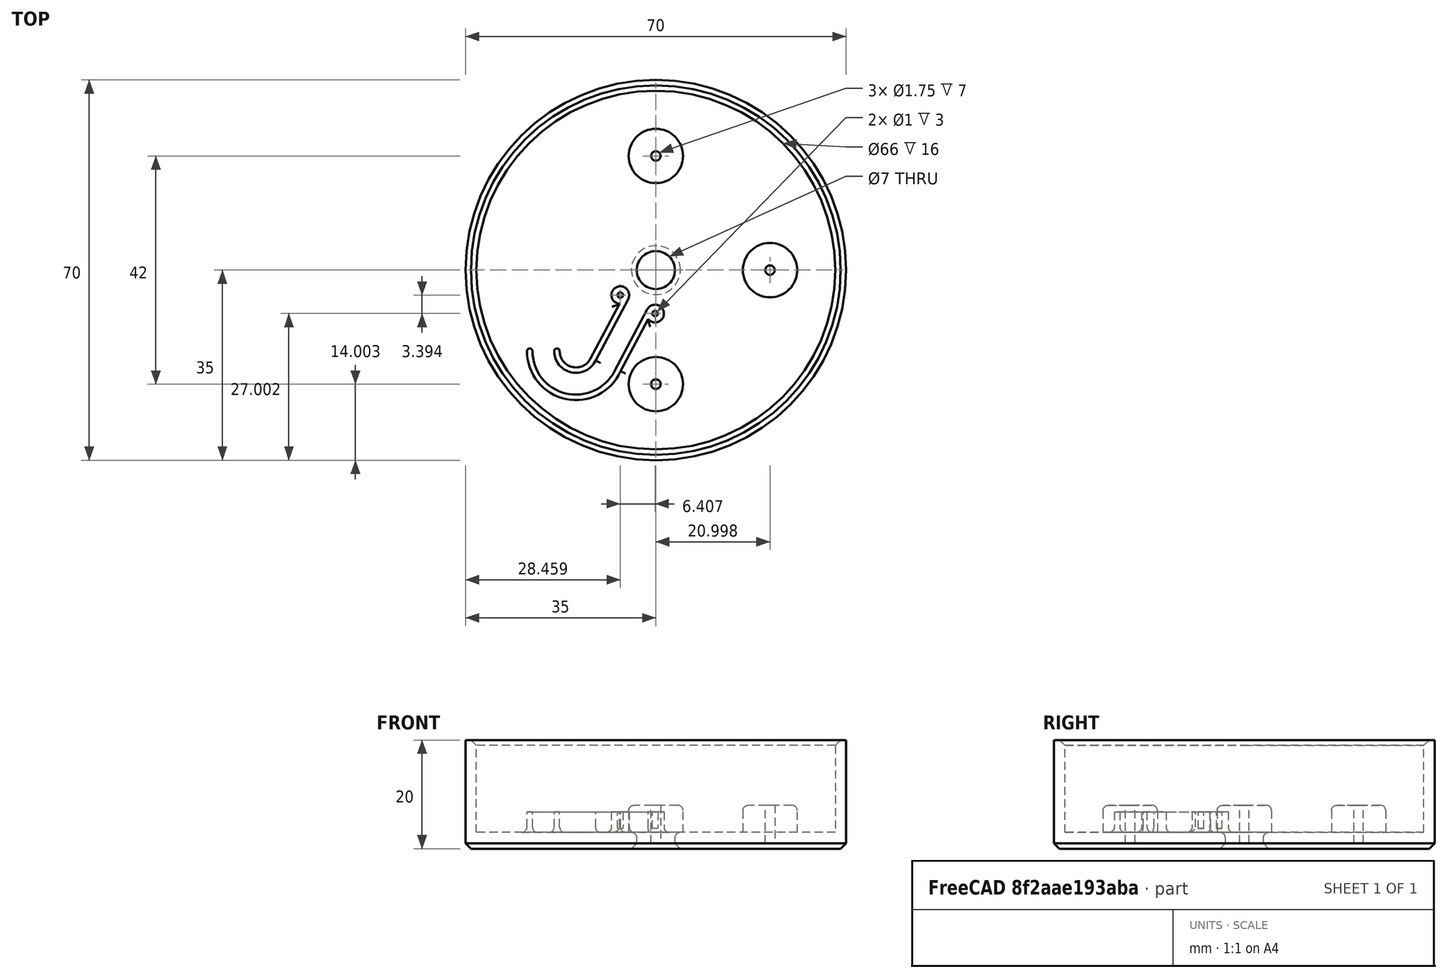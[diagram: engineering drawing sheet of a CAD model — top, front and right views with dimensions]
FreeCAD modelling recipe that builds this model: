
FCSTD DOCUMENT  (FreeCAD 0.21R33771 (Git))
Label: Webcam mount
License: All rights reserved
LicenseURL: http://en.wikipedia.org/wiki/All_rights_reserved
objects: Sketcher::SketchObject×8, PartDesign::Pocket×4, PartDesign::Fillet×4, PartDesign::Pad×3, PartDesign::Body×2, Part::Feature×2, PartDesign::Chamfer×1, App::Part×1, Mesh::Feature×1, Part::Refine×1
note: 37 computed .brp shape members not serialized (recipe doc carries the construction recipe); baked Part::Feature solids carry a one-line shape summary decoded from their .brp

FEATURE [Sketcher::SketchObject] Sketch001
  FullyConstrained = true
  MapMode = 5
  Support = -> [XY_Plane]
  sketch-geometry (1):
    g0: Circle CenterX=0 CenterY=0 CenterZ=0 NormalX=0 NormalY=0 NormalZ=1 AngleXU=0 Radius=35
  constraints (2):
    c: Coincident(g0,g-1)
    c: Diameter(g0) = 70
FEATURE [PartDesign::Pad] Pad
  Direction = (0,0,1)
  Length = 20
  Length2 = 10
  Profile = -> Sketch001
  ReferenceAxis = -> Sketch001 [N_Axis]
  Type = 0
FEATURE [Sketcher::SketchObject] Sketch
  FullyConstrained = true
  MapMode = 5
  Placement = pos=(0,0,20) rot=(0,0,1;0rad)
  Support = -> [Pad]
  sketch-geometry (1):
    g0: Circle CenterX=0 CenterY=0 CenterZ=0 NormalX=0 NormalY=0 NormalZ=1 AngleXU=0 Radius=33
  constraints (2):
    c: Coincident(g0,g-1)
    c: Diameter(g0) = 66
FEATURE [PartDesign::Pocket] Pocket
  BaseFeature = -> Pad
  Direction = (0,0,-1)
  Length = 17
  Length2 = 5
  Profile = -> Sketch
  ReferenceAxis = -> Sketch [N_Axis]
  Type = 0
FEATURE [Sketcher::SketchObject] Sketch002
  FullyConstrained = false
  MapMode = 5
  Placement = pos=(0,0,3) rot=(0,0,1;0rad)
  Support = -> [Pocket]
  sketch-geometry (4):
    g0: Circle CenterX=-0.00194019 CenterY=0.00345167 CenterZ=0 NormalX=0 NormalY=0 NormalZ=1 AngleXU=0 Radius=21
    g1: Circle CenterX=0 CenterY=21.0035 CenterZ=0 NormalX=0 NormalY=0 NormalZ=1 AngleXU=0 Radius=5
    g2: Circle CenterX=20.9981 CenterY=0 CenterZ=0 NormalX=0 NormalY=0 NormalZ=1 AngleXU=0 Radius=5
    g3: Circle CenterX=0 CenterY=-20.9965 CenterZ=0 NormalX=0 NormalY=0 NormalZ=1 AngleXU=0 Radius=5
  constraints (10):
    c: Diameter(g0) = 42
    c: PointOnObject(g1,g0)
    c: PointOnObject(g2,g0)
    c: PointOnObject(g3,g0)
    c: PointOnObject(g3,g-2)
    c: PointOnObject(g2,g-1)
    c: PointOnObject(g1,g-2)
    c: Equal(g1,g2)
    c: Equal(g2,g3)
    c: Diameter(g1) = 10
FEATURE [PartDesign::Pad] Pad001
  BaseFeature = -> Pocket
  Direction = (0,0,1)
  Length = 5
  Length2 = 10
  Profile = -> Sketch002
  ReferenceAxis = -> Sketch002 [N_Axis]
  Type = 0
FEATURE [Sketcher::SketchObject] Sketch003
  ExternalGeometry = -> [Pad001]
  FullyConstrained = true
  MapMode = 5
  Placement = pos=(0,0,8) rot=(0,0,1;0rad)
  Support = -> [Pad001]
  sketch-geometry (3):
    g0: Circle CenterX=0 CenterY=21.0035 CenterZ=0 NormalX=0 NormalY=0 NormalZ=1 AngleXU=0 Radius=0.875
    g1: Circle CenterX=0 CenterY=-20.9965 CenterZ=0 NormalX=0 NormalY=0 NormalZ=1 AngleXU=0 Radius=0.875
    g2: Circle CenterX=20.9981 CenterY=0 CenterZ=0 NormalX=0 NormalY=0 NormalZ=1 AngleXU=0 Radius=0.875
  constraints (6):
    c: Coincident(g0,g-3)
    c: Coincident(g1,g-4)
    c: Coincident(g2,g-5)
    c: Equal(g0,g1)
    c: Equal(g1,g2)
    c: Diameter(g0) = 1.75
FEATURE [PartDesign::Pocket] Pocket001
  BaseFeature = -> Pad001
  Direction = (0,0,-1)
  Length = 7
  Length2 = 5
  Profile = -> Sketch003
  ReferenceAxis = -> Sketch003 [N_Axis]
  Type = 0
FEATURE [Sketcher::SketchObject] Sketch004
  FullyConstrained = true
  MapMode = 5
  Placement = pos=(0,0,3) rot=(0,0,1;0rad)
  Support = -> [Pocket001]
  sketch-geometry (1):
    g0: Circle CenterX=0 CenterY=0 CenterZ=0 NormalX=0 NormalY=0 NormalZ=1 AngleXU=0 Radius=3.5
  constraints (3):
    c: PointOnObject(g0,g-1)
    c: Diameter(g0) = 7
    c: PointOnObject(g0,g-2)
FEATURE [PartDesign::Pocket] Pocket002
  BaseFeature = -> Pocket001
  Direction = (0,0,-1)
  Length = 10
  Length2 = 5
  Profile = -> Sketch004
  ReferenceAxis = -> Sketch004 [N_Axis]
  Type = 0
FEATURE [PartDesign::Chamfer] Chamfer
  Angle = 45
  Base = -> Pocket002 [Edge2,Edge5,Edge4]
  BaseFeature = -> Pocket002
  ChamferType = 0
  FlipDirection = false
  Size = 1
  Size2 = 1
  SupportTransform = false
  UseAllEdges = false
FEATURE [Sketcher::SketchObject] Sketch005
  ExternalGeometry = -> [Chamfer]
  FullyConstrained = false
  MapMode = 5
  Placement = pos=(0,0,3) rot=(0,0,1;0rad)
  Support = -> [Chamfer]
  sketch-geometry (21):
    g0: LineSegment StartX=0 StartY=0 StartZ=0 EndX=-12.3375 EndY=-23.2904 EndZ=0
    g1: LineSegment StartX=-3.33785 StartY=-6.30109 StartZ=0 EndX=-5.10519 EndY=-5.36488 EndZ=0
    g2: LineSegment StartX=-3.33785 StartY=-6.30109 StartZ=0 EndX=-1.5705 EndY=-7.2373 EndZ=0
    g3: ArcOfCircle CenterX=-0.134531 CenterY=-7.99797 CenterZ=0 NormalX=0 NormalY=0 NormalZ=1 AngleXU=0 Radius=1.625 StartAngle=3.81788 EndAngle=8.93763
    g4: ArcOfCircle CenterX=-6.54116 CenterY=-4.60421 CenterZ=0 NormalX=0 NormalY=0 NormalZ=1 AngleXU=0 Radius=1.625 StartAngle=5.79576 EndAngle=10.9054
    g5: ArcOfCircle CenterX=-14.6925 CenterY=-14.9185 CenterZ=0 NormalX=0 NormalY=0 NormalZ=1 AngleXU=0 Radius=4 StartAngle=3.14159 EndAngle=5.83833
    g6: LineSegment StartX=-11.1578 StartY=-16.7909 StartZ=0 EndX=-9.3905 EndY=-17.7271 EndZ=0
    g7: LineSegment StartX=-9.3905 StartY=-17.7271 StartZ=0 EndX=-7.62315 EndY=-18.6633 EndZ=0
    g8: LineSegment StartX=-14.9937 StartY=-18.9071 StartZ=0 EndX=-14.9184 EndY=-17.91 EndZ=0
    g9: ArcOfCircle CenterX=-14.6925 CenterY=-14.9185 CenterZ=0 NormalX=0 NormalY=0 NormalZ=1 AngleXU=0 Radius=3 StartAngle=3.14159 EndAngle=5.79576
    g10: LineSegment StartX=-8.32768 StartY=-19.765 StartZ=0 EndX=-7.53208 EndY=-20.3708 EndZ=0
    g11: LineSegment StartX=-11.0819 StartY=-16.6398 StartZ=0 EndX=-5.10541 EndY=-5.36528 EndZ=0
    g12: LineSegment StartX=-7.62315 StartY=-18.6633 StartZ=0 EndX=-1.5705 EndY=-7.2373 EndZ=0
    g13: LineSegment StartX=-6.48386 StartY=-18.6087 StartZ=0 EndX=-1.40187 EndY=-9.01506 EndZ=0
    g14: LineSegment StartX=-12.0419 StartY=-16.3235 StartZ=0 EndX=-6.68757 EndY=-6.2226 EndZ=0
    g15: LineSegment StartX=-14.6925 StartY=-14.9185 StartZ=0 EndX=-23.6925 EndY=-14.9185 EndZ=0
    g16: ArcOfCircle CenterX=-23.1925 CenterY=-14.9185 CenterZ=0 NormalX=0 NormalY=0 NormalZ=1 AngleXU=0 Radius=0.5 StartAngle=0 EndAngle=3.14159
    g17: ArcOfCircle CenterX=-18.1925 CenterY=-14.9185 CenterZ=0 NormalX=0 NormalY=0 NormalZ=1 AngleXU=0 Radius=0.5 StartAngle=-9e-16 EndAngle=3.14159
    g18: GeomPoint X=-22.6925 Y=-14.9185 Z=0
    g19: ArcOfCircle CenterX=-14.6925 CenterY=-14.9185 CenterZ=0 NormalX=0 NormalY=0 NormalZ=1 AngleXU=0 Radius=9 StartAngle=3.14159 EndAngle=5.86071
    g20: ArcOfCircle CenterX=-14.6925 CenterY=-14.9185 CenterZ=0 NormalX=0 NormalY=0 NormalZ=1 AngleXU=0 Radius=8 StartAngle=3.14159 EndAngle=5.79604
  constraints (45):
    c: Coincident(g0,g-3)
    c: Coincident(g2,g1)
    c: PointOnObject(g1,g0)
    c: Perpendicular(g0,g1)
    c: Perpendicular(g0,g2)
    c: Equal(g1,g2)
    c: Distance(g1,g2) = 4
    c: PointOnObject(g1,g4)
    c: Perpendicular(g4,g1)
    c: Equal(g4,g3)
    c: Diameter(g3) = 3.25
    c: Diameter(g5) = 8
    c: PointOnObject(g6,g5)
    c: Coincident(g7,g6)
    c: Perpendicular(g5,g6)
    c: Equal(g6,g7)
    c: PointOnObject(g6,g0)
    c: Perpendicular(g0,g6)
    c: PointOnObject(g8,g5)
    c: Perpendicular(g5,g8)
    c: Distance(g8) = 1  'cable guide wall thickness'
    c: Coincident(g9,g5)
    c: PointOnObject(g8,g9)
    c: Equal(g8,g10)
    c: Tangent(g12,g3) = 1.5708
    c: Parallel(g14,g11)
    c: Parallel(g12,g13)
    c: Coincident(g15,g5)
    c: Horizontal(g15)
    c: PointOnObject(g16,g15)
    c: PointOnObject(g17,g15)
    c: PointOnObject(g18,g16)
    c: Coincident(g19,g13)
    c: Coincident(g20,g12) = -1.5708
    c: Perpendicular(g3,g2) = 1.5708
    c: Coincident(g3,g13)
    c: Coincident(g4,g14)
    c: Tangent(g4,g11) = -1.5708
    c: Tangent(g16,g19) = -1.5708
    c: Tangent(g16,g20) = 1.5708
    c: Tangent(g17,g9) = 1.5708
    c: Tangent(g5,g17) = -1.5708
    c: Tangent(g9,g14) = -1.5708
    c: PointOnObject(g9,g15)
    c: Coincident(g5,g11)
FEATURE [PartDesign::Pad] Pad002
  BaseFeature = -> Chamfer
  Direction = (0,0,1)
  Length = 3.75
  Length2 = 10
  Profile = -> Sketch005
  ReferenceAxis = -> Sketch005 [N_Axis]
  Type = 0
FEATURE [Sketcher::SketchObject] Sketch006
  ExternalGeometry = -> [Pad002]
  FullyConstrained = true
  MapMode = 5
  Placement = pos=(0,0,6.75) rot=(0,0,1;0rad)
  Support = -> [Pad002]
  sketch-geometry (2):
    g0: Circle CenterX=-6.54116 CenterY=-4.60421 CenterZ=0 NormalX=0 NormalY=0 NormalZ=1 AngleXU=0 Radius=0.5
    g1: Circle CenterX=-0.134531 CenterY=-7.99797 CenterZ=0 NormalX=0 NormalY=0 NormalZ=1 AngleXU=0 Radius=0.5
  constraints (4):
    c: Coincident(g0,g-3)
    c: Coincident(g1,g-4)
    c: Equal(g0,g1)
    c: Diameter(g0) = 1
FEATURE [PartDesign::Pocket] Pocket003
  BaseFeature = -> Pad002
  Direction = (0,0,-1)
  Length = 3
  Length2 = 5
  Profile = -> Sketch006
  ReferenceAxis = -> Sketch006 [N_Axis]
  Type = 0
FEATURE [PartDesign::Fillet] Fillet
  Base = -> Pocket003 [Edge15]
  BaseFeature = -> Pocket003
  Radius = 1
  SupportTransform = false
  UseAllEdges = false
FEATURE [PartDesign::Body] Body001  label="Body"
  Origin = -> Origin002
FEATURE [PartDesign::Fillet] Fillet001
  Base = -> Fillet [Edge21]
  BaseFeature = -> Fillet
  Radius = 1
  SupportTransform = false
  UseAllEdges = false
FEATURE [PartDesign::Fillet] Fillet002
  Base = -> Fillet001 [Edge13]
  BaseFeature = -> Fillet001
  Radius = 1
  SupportTransform = false
  UseAllEdges = false
FEATURE [PartDesign::Fillet] Fillet003
  Base = -> Fillet002 [Edge49,Edge47,Edge51]
  BaseFeature = -> Fillet002
  Radius = 1
  SupportTransform = false
  UseAllEdges = false
FEATURE [PartDesign::Body] Body  label="Webcam Mount"
  Group = -> [Sketch,Sketch001,Pad,Pocket,Sketch002,Pad001,Sketch003,Pocket001,Sketch004,Pocket002,Chamfer,Sketch005,Pad002,Sketch006,Pocket003,Fillet,Fillet001,Fillet002,Fillet003]
  Origin = -> Origin
  Tip = -> Fillet003
FEATURE [App::Part] Part
  Group = -> [Body,Body001]
  Origin = -> Origin001
FEATURE [Mesh::Feature] Head_v1
FEATURE [Part::Feature] Head_v002
  shape: large baked B-rep (101 MB .brp); summary skipped
FEATURE [Part::Refine] Head_v003
  Source = -> Head_v002
FEATURE [Part::Feature] Head_v003_cs
  shape: bbox 3e-07 x 154.9 x 129.2 mm, 0 faces, 0 solids (baked)
FEATURE [Sketcher::SketchObject] Sketch007
  FullyConstrained = false
  Placement = pos=(-1e-16,0,0) rot=(0,1,0;1.5708rad)
  sketch-geometry (958):
    g0: LineSegment StartX=-14.9545 StartY=-9.1568 StartZ=0 EndX=-14.9605 EndY=-13 EndZ=0
    g1: LineSegment StartX=-6.96052 StartY=-13 StartZ=0 EndX=-6.96169 EndY=-9.32042 EndZ=0
    g2: LineSegment StartX=-7.31044 StartY=10.5454 StartZ=0 EndX=-7.50421 EndY=10.5426 EndZ=0
    g3: LineSegment StartX=-7.29579 StartY=10.5452 StartZ=0 EndX=-7.31044 EndY=10.5454 EndZ=0
    g4: LineSegment StartX=-6.25421 StartY=-10.5416 StartZ=0 EndX=-6.10315 EndY=-10.5451 EndZ=0
    g5: LineSegment StartX=-6.10315 StartY=-10.5451 StartZ=0 EndX=-6.04579 EndY=-10.5439 EndZ=0
    g6: LineSegment StartX=-4.98972 StartY=10.5462 StartZ=0 EndX=-5.00421 EndY=10.5459 EndZ=0
    g7: LineSegment StartX=-4.79579 StartY=10.5428 StartZ=0 EndX=-4.98972 EndY=10.5462 EndZ=0
    g8: LineSegment StartX=-3.75421 StartY=-10.5417 StartZ=0 EndX=-3.61516 EndY=-10.5421 EndZ=0
    g9: LineSegment StartX=-3.61516 StartY=-10.5421 StartZ=0 EndX=-3.54579 EndY=-10.5421 EndZ=0
    g10: LineSegment StartX=-2.4 StartY=10.5463 StartZ=0 EndX=-2.50421 EndY=10.5422 EndZ=0
    g11: LineSegment StartX=-9.92799 StartY=10.5384 StartZ=0 EndX=-10.0042 EndY=10.5374 EndZ=0
    g12: LineSegment StartX=-9.79579 StartY=10.5365 StartZ=0 EndX=-9.92799 EndY=10.5384 EndZ=0
    g13: LineSegment StartX=-12.407 StartY=10.538 StartZ=0 EndX=-12.5042 EndY=10.5364 EndZ=0
    g14: LineSegment StartX=-12.2958 StartY=10.5362 StartZ=0 EndX=-12.407 EndY=10.538 EndZ=0
    g15: LineSegment StartX=-6.90762 StartY=9.86667 StartZ=0 EndX=-7.21779 EndY=10.4103 EndZ=0
    g16: LineSegment StartX=-7.21779 StartY=10.4103 StartZ=0 EndX=-7.29579 EndY=10.5452 EndZ=0
    g17: LineSegment StartX=-5.91918 StartY=-10.3263 StartZ=0 EndX=-5.6576 EndY=-9.86975 EndZ=0
    g18: LineSegment StartX=-6.04579 StartY=-10.5439 StartZ=0 EndX=-5.91918 EndY=-10.3263 EndZ=0
    g19: LineSegment StartX=-4.40761 StartY=9.86821 StartZ=0 EndX=-4.64697 EndY=10.2868 EndZ=0
    g20: LineSegment StartX=-4.64697 StartY=10.2868 StartZ=0 EndX=-4.79579 EndY=10.5428 EndZ=0
    g21: LineSegment StartX=-3.38439 StartY=-10.2617 StartZ=0 EndX=-3.15764 EndY=-9.86228 EndZ=0
    g22: LineSegment StartX=-3.54579 StartY=-10.5421 StartZ=0 EndX=-3.38439 EndY=-10.2617 EndZ=0
    g23: LineSegment StartX=-6.65266 StartY=9.42999 StartZ=0 EndX=-6.90762 EndY=9.86667 EndZ=0
    g24: LineSegment StartX=-6.4951 StartY=9.1553 StartZ=0 EndX=-6.65266 EndY=9.42999 EndZ=0
    g25: LineSegment StartX=-5.44946 StartY=-9.50613 StartZ=0 EndX=-5.24511 EndY=-9.14778 EndZ=0
    g26: LineSegment StartX=-5.6576 StartY=-9.86975 StartZ=0 EndX=-5.44946 EndY=-9.50613 EndZ=0
    g27: LineSegment StartX=-4.09732 StartY=9.33501 StartZ=0 EndX=-4.40761 EndY=9.86821 EndZ=0
    g28: LineSegment StartX=-3.9951 StartY=9.1557 StartZ=0 EndX=-4.09732 EndY=9.33501 EndZ=0
    g29: LineSegment StartX=-2.98257 StartY=-9.5606 StartZ=0 EndX=-2.74511 EndY=-9.14769 EndZ=0
    g30: LineSegment StartX=-3.15764 StartY=-9.86228 StartZ=0 EndX=-2.98257 EndY=-9.5606 EndZ=0
    g31: LineSegment StartX=-9.01623 StartY=9.19342 StartZ=0 EndX=-9.20127 EndY=9.50369 EndZ=0
    g32: LineSegment StartX=-8.99511 StartY=9.15713 StartZ=0 EndX=-9.01623 EndY=9.19342 EndZ=0
    g33: LineSegment StartX=-9.61608 StartY=10.2212 StartZ=0 EndX=-9.70019 EndY=10.3732 EndZ=0
    g34: LineSegment StartX=-9.70019 StartY=10.3732 StartZ=0 EndX=-9.79579 EndY=10.5365 EndZ=0
    g35: LineSegment StartX=-9.27735 StartY=9.63476 StartZ=0 EndX=-9.40751 EndY=9.86041 EndZ=0
    g36: LineSegment StartX=-9.20127 StartY=9.50369 StartZ=0 EndX=-9.27735 EndY=9.63476 EndZ=0
    g37: LineSegment StartX=-9.48436 StartY=9.99283 StartZ=0 EndX=-9.61608 EndY=10.2212 EndZ=0
    g38: LineSegment StartX=-9.40751 StartY=9.86041 StartZ=0 EndX=-9.48436 EndY=9.99283 EndZ=0
    g39: LineSegment StartX=-11.5538 StartY=9.25703 StartZ=0 EndX=-11.7014 EndY=9.50627 EndZ=0
    g40: LineSegment StartX=-11.4951 StartY=9.1539 StartZ=0 EndX=-11.5538 EndY=9.25703 EndZ=0
    g41: LineSegment StartX=-11.805 StartY=9.68615 StartZ=0 EndX=-11.9076 EndY=9.86308 EndZ=0
    g42: LineSegment StartX=-11.7014 StartY=9.50627 StartZ=0 EndX=-11.805 EndY=9.68615 EndZ=0
    g43: LineSegment StartX=-12.0094 StartY=10.0397 StartZ=0 EndX=-12.1096 EndY=10.2126 EndZ=0
    g44: LineSegment StartX=-11.9076 StartY=9.86308 StartZ=0 EndX=-12.0094 EndY=10.0397 EndZ=0
    g45: LineSegment StartX=-12.1096 StartY=10.2126 StartZ=0 EndX=-12.1988 EndY=10.3664 EndZ=0
    g46: LineSegment StartX=-12.1988 StartY=10.3664 StartZ=0 EndX=-12.2958 EndY=10.5362 EndZ=0
    g47: LineSegment StartX=-5.8049 StartY=9.15238 StartZ=0 EndX=-6.28745 EndY=9.15846 EndZ=0
    g48: LineSegment StartX=-6.28745 StartY=9.15846 StartZ=0 EndX=-6.4951 EndY=9.1553 EndZ=0
    g49: LineSegment StartX=-5.24511 StartY=-9.14778 StartZ=0 EndX=-4.8517 EndY=-9.15337 EndZ=0
    g50: LineSegment StartX=-4.8517 StartY=-9.15337 StartZ=0 EndX=-4.55489 EndY=-9.15089 EndZ=0
    g51: LineSegment StartX=-3.30489 StartY=9.15771 StartZ=0 EndX=-3.53898 EndY=9.15932 EndZ=0
    g52: LineSegment StartX=-3.53898 StartY=9.15932 StartZ=0 EndX=-3.9951 EndY=9.1557 EndZ=0
    g53: LineSegment StartX=-2.74511 StartY=-9.14769 StartZ=0 EndX=-2.57759 EndY=-9.14941 EndZ=0
    g54: LineSegment StartX=-2.57759 StartY=-9.14941 StartZ=0 EndX=-2.4 EndY=-9.14758 EndZ=0
    g55: LineSegment StartX=-8.30489 StartY=9.15118 StartZ=0 EndX=-8.9275 EndY=9.15775 EndZ=0
    g56: LineSegment StartX=-8.9275 StartY=9.15775 StartZ=0 EndX=-8.99511 EndY=9.15713 EndZ=0
    g57: LineSegment StartX=-10.8049 StartY=9.15757 StartZ=0 EndX=-10.9593 EndY=9.15905 EndZ=0
    g58: LineSegment StartX=-10.9593 StartY=9.15905 StartZ=0 EndX=-11.4951 EndY=9.1539 EndZ=0
    g59: LineSegment StartX=-16.4319 StartY=9.15863 StartZ=0 EndX=-16.4951 EndY=9.15757 EndZ=0
    g60: LineSegment StartX=-15.8049 StartY=9.15155 StartZ=0 EndX=-16.4319 EndY=9.15863 EndZ=0
    g61: LineSegment StartX=-17.7451 StartY=-9.151 StartZ=0 EndX=-17.1528 EndY=-9.15512 EndZ=0
    g62: LineSegment StartX=-17.1528 StartY=-9.15512 StartZ=0 EndX=-17.0549 EndY=-9.15542 EndZ=0
    g63: LineSegment StartX=-18.3049 StartY=9.15402 StartZ=0 EndX=-18.4822 EndY=9.15502 EndZ=0
    g64: LineSegment StartX=-18.4822 StartY=9.15502 StartZ=0 EndX=-18.9951 EndY=9.14798 EndZ=0
    g65: LineSegment StartX=-20.2451 StartY=-9.15255 StartZ=0 EndX=-20.0024 EndY=-9.15661 EndZ=0
    g66: LineSegment StartX=-20.0024 StartY=-9.15661 StartZ=0 EndX=-19.5549 EndY=-9.15178 EndZ=0
    g67: LineSegment StartX=-20.8049 StartY=9.15835 StartZ=0 EndX=-21.4168 EndY=9.1557 EndZ=0
    g68: LineSegment StartX=-21.4168 StartY=9.1557 StartZ=0 EndX=-21.4951 EndY=9.15525 EndZ=0
    g69: LineSegment StartX=-22.3429 StartY=-9.15449 StartZ=0 EndX=-22.0549 EndY=-9.15237 EndZ=0
    g70: LineSegment StartX=-22.7451 StartY=-9.14854 StartZ=0 EndX=-22.3429 EndY=-9.15449 EndZ=0
    g71: LineSegment StartX=-15.0644 StartY=-9.15663 StartZ=0 EndX=-14.9545 EndY=-9.1568 EndZ=0
    g72: LineSegment StartX=-15.2451 StartY=-9.14926 StartZ=0 EndX=-15.0644 EndY=-9.15663 EndZ=0
    g73: LineSegment StartX=-13.5397 StartY=9.15597 StartZ=0 EndX=-13.9951 EndY=9.14854 EndZ=0
    g74: LineSegment StartX=-13.3049 StartY=9.15328 StartZ=0 EndX=-13.5397 EndY=9.15597 EndZ=0
    g75: LineSegment StartX=-7.83785 StartY=9.96766 StartZ=0 EndX=-7.85984 EndY=9.92931 EndZ=0
    g76: LineSegment StartX=-7.50421 StartY=10.5426 StartZ=0 EndX=-7.83785 EndY=9.96766 EndZ=0
    g77: LineSegment StartX=-6.40399 StartY=-10.2802 StartZ=0 EndX=-6.25421 EndY=-10.5416 EndZ=0
    g78: LineSegment StartX=-6.60986 StartY=-9.91758 StartZ=0 EndX=-6.40399 EndY=-10.2802 EndZ=0
    g79: LineSegment StartX=-5.00421 StartY=10.5459 StartZ=0 EndX=-5.18128 EndY=10.2373 EndZ=0
    g80: LineSegment StartX=-5.18128 StartY=10.2373 StartZ=0 EndX=-5.35381 EndY=9.93594 EndZ=0
    g81: LineSegment StartX=-5.35381 StartY=9.93594 StartZ=0 EndX=-5.35988 EndY=9.92531 EndZ=0
    g82: LineSegment StartX=-4.10989 StartY=-9.91607 StartZ=0 EndX=-3.90113 EndY=-10.2847 EndZ=0
    g83: LineSegment StartX=-3.90113 StartY=-10.2847 StartZ=0 EndX=-3.75421 EndY=-10.5417 EndZ=0
    g84: LineSegment StartX=-2.50421 StartY=10.5422 StartZ=0 EndX=-2.80243 EndY=10.0184 EndZ=0
    g85: LineSegment StartX=-2.80243 StartY=10.0184 StartZ=0 EndX=-2.85984 EndY=9.91585 EndZ=0
    g86: LineSegment StartX=-2.85984 StartY=9.91585 StartZ=0 EndX=-3.06478 EndY=9.56799 EndZ=0
    g87: LineSegment StartX=-3.06478 StartY=9.56799 StartZ=0 EndX=-3.30489 EndY=9.15771 EndZ=0
    g88: LineSegment StartX=-4.55489 StartY=-9.15089 StartZ=0 EndX=-4.3434 EndY=-9.51836 EndZ=0
    g89: LineSegment StartX=-4.3434 StartY=-9.51836 StartZ=0 EndX=-4.10989 EndY=-9.91607 EndZ=0
    g90: LineSegment StartX=-5.35988 StartY=9.92531 StartZ=0 EndX=-5.38292 EndY=9.8858 EndZ=0
    g91: LineSegment StartX=-5.38292 StartY=9.8858 StartZ=0 EndX=-5.8049 EndY=9.15238 EndZ=0
    g92: LineSegment StartX=-6.91617 StartY=-9.39768 StartZ=0 EndX=-6.60986 EndY=-9.91758 EndZ=0
    g93: LineSegment StartX=-6.96169 StartY=-9.32042 StartZ=0 EndX=-6.91617 EndY=-9.39768 EndZ=0
    g94: LineSegment StartX=-7.8759 StartY=9.90176 StartZ=0 EndX=-8.30489 EndY=9.15118 EndZ=0
    g95: LineSegment StartX=-7.85984 StartY=9.92931 StartZ=0 EndX=-7.8759 EndY=9.90176 EndZ=0
    g96: LineSegment StartX=-10.7866 StartY=9.18631 StartZ=0 EndX=-10.8049 EndY=9.15757 EndZ=0
    g97: LineSegment StartX=-10.5824 StartY=9.49602 StartZ=0 EndX=-10.7866 EndY=9.18631 EndZ=0
    g98: LineSegment StartX=-10.3599 StartY=9.87949 StartZ=0 EndX=-10.4379 EndY=9.74564 EndZ=0
    g99: LineSegment StartX=-10.4379 StartY=9.74564 StartZ=0 EndX=-10.5824 EndY=9.49602 EndZ=0
    g100: LineSegment StartX=-10.1699 StartY=10.207 StartZ=0 EndX=-10.2358 EndY=10.0938 EndZ=0
    g101: LineSegment StartX=-10.2358 StartY=10.0938 StartZ=0 EndX=-10.3599 EndY=9.87949 EndZ=0
    g102: LineSegment StartX=-10.0042 StartY=10.5374 StartZ=0 EndX=-10.0614 EndY=10.4235 EndZ=0
    g103: LineSegment StartX=-10.0614 StartY=10.4235 StartZ=0 EndX=-10.1699 EndY=10.207 EndZ=0
    g104: LineSegment StartX=-12.6736 StartY=10.239 StartZ=0 EndX=-12.6766 EndY=10.2333 EndZ=0
    g105: LineSegment StartX=-12.5042 StartY=10.5364 StartZ=0 EndX=-12.6736 EndY=10.239 EndZ=0
    g106: LineSegment StartX=-13.0938 StartY=9.51274 StartZ=0 EndX=-13.3049 EndY=9.15328 EndZ=0
    g107: LineSegment StartX=-13.0823 StartY=9.53167 StartZ=0 EndX=-13.0938 EndY=9.51274 EndZ=0
    g108: LineSegment StartX=-12.8578 StartY=9.91994 StartZ=0 EndX=-12.8598 EndY=9.91655 EndZ=0
    g109: LineSegment StartX=-12.6766 StartY=10.2333 StartZ=0 EndX=-12.8578 EndY=9.91994 EndZ=0
    g110: LineSegment StartX=-13.0798 StartY=9.536 StartZ=0 EndX=-13.0823 EndY=9.53167 EndZ=0
    g111: LineSegment StartX=-12.8598 StartY=9.91655 StartZ=0 EndX=-13.0798 EndY=9.536 EndZ=0
    g112: LineSegment StartX=-80.606 StartY=60.5139 StartZ=0 EndX=-79.2709 EndY=59.6757 EndZ=0
    g113: LineSegment StartX=-81.4956 StartY=61.0589 StartZ=0 EndX=-80.606 EndY=60.5139 EndZ=0
    g114: LineSegment StartX=-72.2913 StartY=54.9951 StartZ=0 EndX=-71.4958 EndY=54.4025 EndZ=0
    g115: LineSegment StartX=-72.6704 StartY=55.2677 StartZ=0 EndX=-72.2913 EndY=54.9951 EndZ=0
    g116: LineSegment StartX=-70.9748 StartY=54.0145 StartZ=0 EndX=-70.212 EndY=53.4213 EndZ=0
    g117: LineSegment StartX=-71.4958 StartY=54.4025 StartZ=0 EndX=-70.9748 EndY=54.0145 EndZ=0
    g118: LineSegment StartX=-27.4144 StartY=28.6446 StartZ=0 EndX=-26.4182 EndY=28.4287 EndZ=0
    g119: LineSegment StartX=-28.0613 StartY=28.7968 StartZ=0 EndX=-27.4144 EndY=28.6446 EndZ=0
    g120: LineSegment StartX=-23.9792 StartY=27.9309 StartZ=0 EndX=-23.7287 EndY=27.8804 EndZ=0
    g121: LineSegment StartX=-24.0876 StartY=27.9522 StartZ=0 EndX=-23.9792 EndY=27.9309 EndZ=0
    g122: LineSegment StartX=-6.8106 StartY=25.5322 StartZ=0 EndX=-6.11261 EndY=25.4629 EndZ=0
    g123: LineSegment StartX=-6.11261 StartY=25.4629 StartZ=0 EndX=-5.09184 EndY=25.371 EndZ=0
    g124: LineSegment StartX=-2.77858 StartY=25.1794 StartZ=0 EndX=-2.77693 EndY=25.1793 EndZ=0
    g125: LineSegment StartX=-2.77693 StartY=25.1793 StartZ=0 EndX=-2.77627 EndY=25.1792 EndZ=0
    g126: LineSegment StartX=-7.89257 StartY=25.639 StartZ=0 EndX=-7.86472 EndY=25.6369 EndZ=0
    g127: LineSegment StartX=-7.96277 StartY=25.643 StartZ=0 EndX=-7.89257 EndY=25.639 EndZ=0
    g128: LineSegment StartX=-78.6749 StartY=-59.3066 StartZ=0 EndX=-81.5296 EndY=-61.0864 EndZ=0
    g129: LineSegment StartX=-54.4975 StartY=-39.5637 StartZ=0 EndX=-55.5874 EndY=-40.3942 EndZ=0
    g130: LineSegment StartX=-53.3866 StartY=-38.7705 StartZ=0 EndX=-54.4975 EndY=-39.5637 EndZ=0
    g131: LineSegment StartX=-49.9431 StartY=-36.6436 StartZ=0 EndX=-51.1075 EndY=-37.3093 EndZ=0
    g132: LineSegment StartX=-51.1075 StartY=-37.3093 StartZ=0 EndX=-52.256 EndY=-38.0184 EndZ=0
    g133: LineSegment StartX=-52.256 StartY=-38.0184 StartZ=0 EndX=-53.3866 EndY=-38.7705 EndZ=0
    g134: LineSegment StartX=-55.5874 StartY=-40.3942 StartZ=0 EndX=-56.656 EndY=-41.2571 EndZ=0
    g135: LineSegment StartX=-56.656 StartY=-41.2571 StartZ=0 EndX=-57.7034 EndY=-42.1466 EndZ=0
    g136: LineSegment StartX=-57.7034 StartY=-42.1466 StartZ=0 EndX=-58.7305 EndY=-43.0563 EndZ=0
    g137: LineSegment StartX=-58.7305 StartY=-43.0563 StartZ=0 EndX=-60.7321 EndY=-44.9114 EndZ=0
    g138: LineSegment StartX=-60.7321 StartY=-44.9114 StartZ=0 EndX=-62.6855 EndY=-46.7769 EndZ=0
    g139: LineSegment StartX=-62.6855 StartY=-46.7769 StartZ=0 EndX=-64.631 EndY=-48.6222 EndZ=0
    g140: LineSegment StartX=-64.631 StartY=-48.6222 StartZ=0 EndX=-66.6206 EndY=-50.4365 EndZ=0
    g141: LineSegment StartX=-66.6206 StartY=-50.4365 StartZ=0 EndX=-67.6491 EndY=-51.3326 EndZ=0
    g142: LineSegment StartX=-67.6491 StartY=-51.3326 StartZ=0 EndX=-68.7087 EndY=-52.2228 EndZ=0
    g143: LineSegment StartX=-68.7087 StartY=-52.2228 StartZ=0 EndX=-69.805 EndY=-53.1089 EndZ=0
    g144: LineSegment StartX=-69.805 StartY=-53.1089 StartZ=0 EndX=-70.9424 EndY=-53.9925 EndZ=0
    g145: LineSegment StartX=-70.9424 StartY=-53.9925 StartZ=0 EndX=-72.1237 EndY=-54.8752 EndZ=0
    g146: LineSegment StartX=-72.1237 StartY=-54.8752 StartZ=0 EndX=-73.3503 EndY=-55.7583 EndZ=0
    g147: LineSegment StartX=-73.3503 StartY=-55.7583 StartZ=0 EndX=-74.6215 EndY=-56.6428 EndZ=0
    g148: LineSegment StartX=-74.6215 StartY=-56.6428 StartZ=0 EndX=-75.9352 EndY=-57.529 EndZ=0
    g149: LineSegment StartX=-75.9352 StartY=-57.529 StartZ=0 EndX=-77.2879 EndY=-58.4171 EndZ=0
    g150: LineSegment StartX=-77.2879 StartY=-58.4171 StartZ=0 EndX=-78.6749 EndY=-59.3066 EndZ=0
    g151: LineSegment StartX=-81.5296 StartY=-61.0864 StartZ=0 EndX=-84.4501 EndY=-62.8562 EndZ=0
    g152: LineSegment StartX=-84.4501 StartY=-62.8562 StartZ=0 EndX=-87.3858 EndY=-64.5964 EndZ=0
    g153: LineSegment StartX=-87.3858 StartY=-64.5964 StartZ=0 EndX=-90.2924 EndY=-66.2799 EndZ=0
    g154: LineSegment StartX=-90.2924 StartY=-66.2799 StartZ=0 EndX=-91.7241 EndY=-67.0901 EndZ=0
    g155: LineSegment StartX=-91.7241 StartY=-67.0901 StartZ=0 EndX=-93.1374 EndY=-67.8736 EndZ=0
    g156: LineSegment StartX=-93.1374 StartY=-67.8736 StartZ=0 EndX=-94.5302 EndY=-68.6261 EndZ=0
    g157: LineSegment StartX=-94.5302 StartY=-68.6261 StartZ=0 EndX=-95.9014 EndY=-69.3438 EndZ=0
    g158: LineSegment StartX=-95.9014 StartY=-69.3438 StartZ=0 EndX=-97.2505 EndY=-70.0234 EndZ=0
    g159: LineSegment StartX=-97.2505 StartY=-70.0234 StartZ=0 EndX=-98.5778 EndY=-70.6623 EndZ=0
    g160: LineSegment StartX=-98.5778 StartY=-70.6623 StartZ=0 EndX=-99.8846 EndY=-71.2591 EndZ=0
    g161: LineSegment StartX=-99.8846 StartY=-71.2591 StartZ=0 EndX=-101.173 EndY=-71.8131 EndZ=0
    g162: LineSegment StartX=-101.173 StartY=-71.8131 StartZ=0 EndX=-102.445 EndY=-72.3254 EndZ=0
    g163: LineSegment StartX=-102.445 StartY=-72.3254 StartZ=0 EndX=-103.705 EndY=-72.7983 EndZ=0
    g164: LineSegment StartX=-103.705 StartY=-72.7983 StartZ=0 EndX=-104.957 EndY=-73.2352 EndZ=0
    g165: LineSegment StartX=-104.957 StartY=-73.2352 StartZ=0 EndX=-106.205 EndY=-73.6408 EndZ=0
    g166: LineSegment StartX=-106.205 StartY=-73.6408 StartZ=0 EndX=-108.703 EndY=-74.3777 EndZ=0
    g167: LineSegment StartX=-108.703 StartY=-74.3777 StartZ=0 EndX=-111.224 EndY=-75.0461 EndZ=0
    g168: LineSegment StartX=-111.224 StartY=-75.0461 StartZ=0 EndX=-113.772 EndY=-75.671 EndZ=0
    g169: LineSegment StartX=-113.772 StartY=-75.671 StartZ=0 EndX=-116.32 EndY=-76.2523 EndZ=0
    g170: LineSegment StartX=-116.32 StartY=-76.2523 StartZ=0 EndX=-117.577 EndY=-76.5191 EndZ=0
    g171: LineSegment StartX=-117.577 StartY=-76.5191 StartZ=0 EndX=-118.812 EndY=-76.7635 EndZ=0
    g172: LineSegment StartX=-118.812 StartY=-76.7635 StartZ=0 EndX=-120.015 EndY=-76.9797 EndZ=0
    g173: LineSegment StartX=-120.015 StartY=-76.9797 StartZ=0 EndX=-121.178 EndY=-77.162 EndZ=0
    g174: LineSegment StartX=-121.178 StartY=-77.162 StartZ=0 EndX=-122.291 EndY=-77.3046 EndZ=0
    g175: LineSegment StartX=-122.291 StartY=-77.3046 StartZ=0 EndX=-123.347 EndY=-77.4025 EndZ=0
    g176: LineSegment StartX=-123.347 StartY=-77.4025 StartZ=0 EndX=-124.341 EndY=-77.4517 EndZ=0
    g177: LineSegment StartX=-124.341 StartY=-77.4517 StartZ=0 EndX=-125.267 EndY=-77.4494 EndZ=0
    g178: LineSegment StartX=-125.267 StartY=-77.4494 StartZ=0 EndX=-126.124 EndY=-77.3938 EndZ=0
    g179: LineSegment StartX=-126.124 StartY=-77.3938 StartZ=0 EndX=-126.91 EndY=-77.2839 EndZ=0
    g180: LineSegment StartX=-83.7605 StartY=62.4361 StartZ=0 EndX=-82.8605 EndY=61.8951 EndZ=0
    g181: LineSegment StartX=-82.8605 StartY=61.8951 StartZ=0 EndX=-81.4956 EndY=61.0589 EndZ=0
    g182: LineSegment StartX=-86.0419 StartY=63.7985 StartZ=0 EndX=-85.1405 EndY=63.2656 EndZ=0
    g183: LineSegment StartX=-85.1405 StartY=63.2656 StartZ=0 EndX=-83.7605 EndY=62.4361 EndZ=0
    g184: LineSegment StartX=-88.3175 StartY=65.1345 StartZ=0 EndX=-87.4228 EndY=64.6148 EndZ=0
    g185: LineSegment StartX=-87.4228 StartY=64.6148 StartZ=0 EndX=-86.0419 EndY=63.7985 EndZ=0
    g186: LineSegment StartX=-98.8055 StartY=70.7592 StartZ=0 EndX=-98.1688 EndY=70.4653 EndZ=0
    g187: LineSegment StartX=-98.1688 StartY=70.4653 StartZ=0 EndX=-97.1846 EndY=69.982 EndZ=0
    g188: LineSegment StartX=-100.396 StartY=71.4736 StartZ=0 EndX=-99.7705 EndY=71.2048 EndZ=0
    g189: LineSegment StartX=-99.7705 StartY=71.2048 StartZ=0 EndX=-98.8055 EndY=70.7592 EndZ=0
    g190: LineSegment StartX=-101.961 StartY=72.1249 StartZ=0 EndX=-101.344 EndY=71.8806 EndZ=0
    g191: LineSegment StartX=-101.344 StartY=71.8806 StartZ=0 EndX=-100.396 EndY=71.4736 EndZ=0
    g192: LineSegment StartX=-117.903 StartY=76.5798 StartZ=0 EndX=-117.463 EndY=76.4918 EndZ=0
    g193: LineSegment StartX=-117.463 StartY=76.4918 StartZ=0 EndX=-116.112 EndY=76.1975 EndZ=0
    g194: LineSegment StartX=-118.995 StartY=76.7918 StartZ=0 EndX=-118.564 EndY=76.7123 EndZ=0
    g195: LineSegment StartX=-118.564 StartY=76.7123 StartZ=0 EndX=-117.903 EndY=76.5798 EndZ=0
    g196: LineSegment StartX=-120.06 StartY=76.9808 StartZ=0 EndX=-119.642 EndY=76.9114 EndZ=0
    g197: LineSegment StartX=-119.642 StartY=76.9114 StartZ=0 EndX=-118.995 EndY=76.7918 EndZ=0
    g198: LineSegment StartX=-121.093 StartY=77.1429 StartZ=0 EndX=-120.689 EndY=77.0852 EndZ=0
    g199: LineSegment StartX=-120.689 StartY=77.0852 StartZ=0 EndX=-120.06 EndY=76.9808 EndZ=0
    g200: LineSegment StartX=-122.088 StartY=77.2739 StartZ=0 EndX=-121.701 EndY=77.2295 EndZ=0
    g201: LineSegment StartX=-121.701 StartY=77.2295 StartZ=0 EndX=-121.093 EndY=77.1429 EndZ=0
    g202: LineSegment StartX=-123.039 StartY=77.3703 StartZ=0 EndX=-122.67 EndY=77.3405 EndZ=0
    g203: LineSegment StartX=-122.67 StartY=77.3405 StartZ=0 EndX=-122.088 EndY=77.2739 EndZ=0
    g204: LineSegment StartX=-126.863 StartY=77.2903 StartZ=0 EndX=-126.173 EndY=77.3849 EndZ=0
    g205: LineSegment StartX=-126.91 StartY=77.2834 StartZ=0 EndX=-126.863 EndY=77.2903 EndZ=0
    g206: LineSegment StartX=-24.9431 StartY=-28.1211 StartZ=0 EndX=-23.7287 EndY=-27.8854 EndZ=0
    g207: LineSegment StartX=-6.61764 StartY=-25.5127 StartZ=0 EndX=-5.30387 EndY=-25.3893 EndZ=0
    g208: LineSegment StartX=-7.96277 StartY=-25.6484 StartZ=0 EndX=-6.61764 EndY=-25.5127 EndZ=0
    g209: LineSegment StartX=-5.30387 StartY=-25.3893 StartZ=0 EndX=-4.02307 EndY=-25.2785 EndZ=0
    g210: LineSegment StartX=-4.02307 StartY=-25.2785 StartZ=0 EndX=-2.77627 EndY=-25.1802 EndZ=0
    g211: LineSegment StartX=-4.4154 StartY=25.3101 StartZ=0 EndX=-2.77858 EndY=25.1794 EndZ=0
    g212: LineSegment StartX=-5.09184 StartY=25.371 StartZ=0 EndX=-4.4154 EndY=25.3101 EndZ=0
    g213: LineSegment StartX=-96.5358 StartY=69.6634 StartZ=0 EndX=-95.5314 EndY=69.1444 EndZ=0
    g214: LineSegment StartX=-97.1846 StartY=69.982 StartZ=0 EndX=-96.5358 EndY=69.6634 EndZ=0
    g215: LineSegment StartX=-115.216 StartY=76.0026 StartZ=0 EndX=-113.338 EndY=75.5562 EndZ=0
    g216: LineSegment StartX=-116.112 StartY=76.1975 StartZ=0 EndX=-115.216 EndY=76.0026 EndZ=0
    g217: LineSegment StartX=-78.4012 StartY=59.1297 StartZ=0 EndX=-77.1098 EndY=58.2924 EndZ=0
    g218: LineSegment StartX=-79.2709 StartY=59.6757 StartZ=0 EndX=-78.4012 EndY=59.1297 EndZ=0
    g219: LineSegment StartX=-76.2689 StartY=57.7473 StartZ=0 EndX=-75.0325 EndY=56.9125 EndZ=0
    g220: LineSegment StartX=-77.1098 StartY=58.2924 StartZ=0 EndX=-76.2689 EndY=57.7473 EndZ=0
    g221: LineSegment StartX=-94.87 StartY=68.8028 StartZ=0 EndX=-93.8455 EndY=68.2515 EndZ=0
    g222: LineSegment StartX=-95.5314 StartY=69.1444 StartZ=0 EndX=-94.87 EndY=68.8028 EndZ=0
    g223: LineSegment StartX=-112.098 StartY=75.2615 StartZ=0 EndX=-110.237 EndY=74.7776 EndZ=0
    g224: LineSegment StartX=-113.338 StartY=75.5562 StartZ=0 EndX=-112.098 EndY=75.2615 EndZ=0
    g225: LineSegment StartX=-74.228 StartY=56.3692 StartZ=0 EndX=-73.636 EndY=55.9547 EndZ=0
    g226: LineSegment StartX=-75.0325 StartY=56.9125 StartZ=0 EndX=-74.228 EndY=56.3692 EndZ=0
    g227: LineSegment StartX=-93.1716 StartY=67.8889 StartZ=0 EndX=-92.1283 EndY=67.3095 EndZ=0
    g228: LineSegment StartX=-93.8455 StartY=68.2515 StartZ=0 EndX=-93.1716 EndY=67.8889 EndZ=0
    g229: LineSegment StartX=-109.009 StartY=74.4584 StartZ=0 EndX=-108.089 EndY=74.1973 EndZ=0
    g230: LineSegment StartX=-110.237 StartY=74.7776 StartZ=0 EndX=-109.009 EndY=74.4584 EndZ=0
    g231: LineSegment StartX=-126.173 StartY=77.3849 StartZ=0 EndX=-125.694 EndY=77.419 EndZ=0
    g232: LineSegment StartX=-91.4426 StartY=66.9287 StartZ=0 EndX=-90.3829 EndY=66.3257 EndZ=0
    g233: LineSegment StartX=-92.1283 StartY=67.3095 StartZ=0 EndX=-91.4426 EndY=66.9287 EndZ=0
    g234: LineSegment StartX=-107.48 StartY=74.0243 StartZ=0 EndX=-106.563 EndY=73.744 EndZ=0
    g235: LineSegment StartX=-108.089 StartY=74.1973 StartZ=0 EndX=-107.48 EndY=74.0243 EndZ=0
    g236: LineSegment StartX=-125.374 StartY=77.4417 StartZ=0 EndX=-124.858 EndY=77.4475 EndZ=0
    g237: LineSegment StartX=-125.694 StartY=77.419 StartZ=0 EndX=-125.374 EndY=77.4417 EndZ=0
    g238: LineSegment StartX=-66.201 StartY=50.0597 StartZ=0 EndX=-65.5327 EndY=49.4504 EndZ=0
    g239: LineSegment StartX=-65.5327 StartY=49.4504 StartZ=0 EndX=-65.0962 EndY=49.0524 EndZ=0
    g240: LineSegment StartX=-65.0962 StartY=49.0524 StartZ=0 EndX=-63.7745 EndY=47.8053 EndZ=0
    g241: LineSegment StartX=-63.7745 StartY=47.8053 StartZ=0 EndX=-62.9301 EndY=47.0085 EndZ=0
    g242: LineSegment StartX=-62.9301 StartY=47.0085 StartZ=0 EndX=-61.8765 EndY=46.0007 EndZ=0
    g243: LineSegment StartX=-61.8765 StartY=46.0007 StartZ=0 EndX=-61.1988 EndY=45.3524 EndZ=0
    g244: LineSegment StartX=-61.1988 StartY=45.3524 StartZ=0 EndX=-60.1252 EndY=44.3445 EndZ=0
    g245: LineSegment StartX=-60.1252 StartY=44.3445 StartZ=0 EndX=-59.4357 EndY=43.6971 EndZ=0
    g246: LineSegment StartX=-59.4357 StartY=43.6971 StartZ=0 EndX=-58.33 EndY=42.7075 EndZ=0
    g247: LineSegment StartX=-58.33 StartY=42.7075 StartZ=0 EndX=-57.6202 EndY=42.0724 EndZ=0
    g248: LineSegment StartX=-57.6202 StartY=42.0724 StartZ=0 EndX=-57.0573 EndY=41.5948 EndZ=0
    g249: LineSegment StartX=-57.0573 StartY=41.5948 StartZ=0 EndX=-56.689 EndY=41.2824 EndZ=0
    g250: LineSegment StartX=-56.689 StartY=41.2824 StartZ=0 EndX=-56.1159 EndY=40.8175 EndZ=0
    g251: LineSegment StartX=-56.1159 StartY=40.8175 StartZ=0 EndX=-55.741 EndY=40.5133 EndZ=0
    g252: LineSegment StartX=-55.741 StartY=40.5133 StartZ=0 EndX=-55.1578 EndY=40.0636 EndZ=0
    g253: LineSegment StartX=-55.1578 StartY=40.0636 StartZ=0 EndX=-54.7761 EndY=39.7692 EndZ=0
    g254: LineSegment StartX=-54.7761 StartY=39.7692 StartZ=0 EndX=-54.183 EndY=39.3368 EndZ=0
    g255: LineSegment StartX=-54.183 StartY=39.3368 StartZ=0 EndX=-53.7946 EndY=39.0536 EndZ=0
    g256: LineSegment StartX=-53.7946 StartY=39.0536 StartZ=0 EndX=-53.1919 EndY=38.6403 EndZ=0
    g257: LineSegment StartX=-53.1919 StartY=38.6403 StartZ=0 EndX=-52.7971 EndY=38.3695 EndZ=0
    g258: LineSegment StartX=-52.7971 StartY=38.3695 StartZ=0 EndX=-52.1855 EndY=37.9765 EndZ=0
    g259: LineSegment StartX=-52.1855 StartY=37.9765 StartZ=0 EndX=-51.7846 EndY=37.7189 EndZ=0
    g260: LineSegment StartX=-51.7846 StartY=37.7189 StartZ=0 EndX=-51.165 EndY=37.3467 EndZ=0
    g261: LineSegment StartX=-51.165 StartY=37.3467 StartZ=0 EndX=-50.7587 EndY=37.1026 EndZ=0
    g262: LineSegment StartX=-50.7587 StartY=37.1026 StartZ=0 EndX=-50.132 EndY=36.7511 EndZ=0
    g263: LineSegment StartX=-50.132 StartY=36.7511 StartZ=0 EndX=-49.7208 EndY=36.5204 EndZ=0
    g264: LineSegment StartX=-49.7208 StartY=36.5204 StartZ=0 EndX=-49.0883 EndY=36.1888 EndZ=0
    g265: LineSegment StartX=-49.0883 StartY=36.1888 StartZ=0 EndX=-48.6729 EndY=35.971 EndZ=0
    g266: LineSegment StartX=-48.6729 StartY=35.971 StartZ=0 EndX=-48.0358 EndY=35.6581 EndZ=0
    g267: LineSegment StartX=-48.0358 StartY=35.6581 StartZ=0 EndX=-47.6172 EndY=35.4525 EndZ=0
    g268: LineSegment StartX=-47.6172 StartY=35.4525 StartZ=0 EndX=-46.9766 EndY=35.1567 EndZ=0
    g269: LineSegment StartX=-46.9766 StartY=35.1567 StartZ=0 EndX=-46.5555 EndY=34.9622 EndZ=0
    g270: LineSegment StartX=-46.5555 StartY=34.9622 StartZ=0 EndX=-45.9128 EndY=34.6816 EndZ=0
    g271: LineSegment StartX=-45.9128 StartY=34.6816 StartZ=0 EndX=-45.49 EndY=34.4971 EndZ=0
    g272: LineSegment StartX=-45.49 StartY=34.4971 StartZ=0 EndX=-44.1959 EndY=33.9714 EndZ=0
    g273: LineSegment StartX=-44.1959 StartY=33.9714 StartZ=0 EndX=-43.3548 EndY=33.6298 EndZ=0
    g274: LineSegment StartX=-43.3548 StartY=33.6298 StartZ=0 EndX=-42.3885 EndY=33.2627 EndZ=0
    g275: LineSegment StartX=-42.3885 StartY=33.2627 StartZ=0 EndX=-41.756 EndY=33.0225 EndZ=0
    g276: LineSegment StartX=-41.756 StartY=33.0225 StartZ=0 EndX=-40.7934 EndY=32.6723 EndZ=0
    g277: LineSegment StartX=-40.7934 StartY=32.6723 StartZ=0 EndX=-40.1629 EndY=32.4429 EndZ=0
    g278: LineSegment StartX=-40.1629 StartY=32.4429 StartZ=0 EndX=-38.2367 EndY=31.7786 EndZ=0
    g279: LineSegment StartX=-38.2367 StartY=31.7786 StartZ=0 EndX=-36.9958 EndY=31.3506 EndZ=0
    g280: LineSegment StartX=-36.9958 StartY=31.3506 StartZ=0 EndX=-35.0766 EndY=30.7393 EndZ=0
    g281: LineSegment StartX=-35.0766 StartY=30.7393 StartZ=0 EndX=-33.8381 EndY=30.3448 EndZ=0
    g282: LineSegment StartX=-33.8381 StartY=30.3448 StartZ=0 EndX=-32.8809 EndY=30.0633 EndZ=0
    g283: LineSegment StartX=-32.8809 StartY=30.0633 StartZ=0 EndX=-32.2526 EndY=29.8786 EndZ=0
    g284: LineSegment StartX=-32.2526 StartY=29.8786 StartZ=0 EndX=-31.2891 EndY=29.6136 EndZ=0
    g285: LineSegment StartX=-31.2891 StartY=29.6136 StartZ=0 EndX=-30.6563 EndY=29.4395 EndZ=0
    g286: LineSegment StartX=-30.6563 StartY=29.4395 StartZ=0 EndX=-29.6839 EndY=29.1914 EndZ=0
    g287: LineSegment StartX=-29.6839 StartY=29.1914 StartZ=0 EndX=-29.0448 EndY=29.0283 EndZ=0
    g288: LineSegment StartX=-29.0448 StartY=29.0283 StartZ=0 EndX=-28.0613 EndY=28.7968 EndZ=0
    g289: LineSegment StartX=-69.7127 StartY=53.033 StartZ=0 EndX=-68.9801 EndY=52.4377 EndZ=0
    g290: LineSegment StartX=-70.212 StartY=53.4213 StartZ=0 EndX=-69.7127 EndY=53.033 EndZ=0
    g291: LineSegment StartX=-105.955 StartY=73.5583 StartZ=0 EndX=-105.037 EndY=73.2532 EndZ=0
    g292: LineSegment StartX=-106.563 StartY=73.744 StartZ=0 EndX=-105.955 EndY=73.5583 EndZ=0
    g293: LineSegment StartX=-124.513 StartY=77.4513 StartZ=0 EndX=-123.961 EndY=77.4295 EndZ=0
    g294: LineSegment StartX=-124.858 StartY=77.4475 StartZ=0 EndX=-124.513 EndY=77.4513 EndZ=0
    g295: LineSegment StartX=-67.3328 StartY=51.0578 StartZ=0 EndX=-66.6484 EndY=50.4542 EndZ=0
    g296: LineSegment StartX=-66.6484 StartY=50.4542 StartZ=0 EndX=-66.201 EndY=50.0597 EndZ=0
    g297: LineSegment StartX=-102.895 StartY=72.4945 StartZ=0 EndX=-101.961 EndY=72.1249 EndZ=0
    g298: LineSegment StartX=-25.7624 StartY=28.2866 StartZ=0 EndX=-24.7528 EndY=28.085 EndZ=0
    g299: LineSegment StartX=-26.4182 StartY=28.4287 StartZ=0 EndX=-25.7624 EndY=28.2866 EndZ=0
    g300: LineSegment StartX=-68.5008 StartY=52.0482 StartZ=0 EndX=-67.7946 EndY=51.4494 EndZ=0
    g301: LineSegment StartX=-68.9801 StartY=52.4377 StartZ=0 EndX=-68.5008 EndY=52.0482 EndZ=0
    g302: LineSegment StartX=-67.7946 StartY=51.4494 StartZ=0 EndX=-67.3328 EndY=51.0578 EndZ=0
    g303: LineSegment StartX=-73.636 StartY=55.9547 StartZ=0 EndX=-73.2461 EndY=55.6817 EndZ=0
    g304: LineSegment StartX=-73.2461 StartY=55.6817 StartZ=0 EndX=-72.6704 EndY=55.2677 EndZ=0
    g305: LineSegment StartX=-90.3829 StartY=66.3257 StartZ=0 EndX=-89.6869 EndY=65.9297 EndZ=0
    g306: LineSegment StartX=-89.6869 StartY=65.9297 StartZ=0 EndX=-88.3175 EndY=65.1345 EndZ=0
    g307: LineSegment StartX=-104.43 StartY=73.0512 StartZ=0 EndX=-103.506 EndY=72.7162 EndZ=0
    g308: LineSegment StartX=-105.037 StartY=73.2532 StartZ=0 EndX=-104.43 EndY=73.0512 EndZ=0
    g309: LineSegment StartX=-103.506 StartY=72.7162 StartZ=0 EndX=-102.895 EndY=72.4945 EndZ=0
    g310: LineSegment StartX=-123.961 StartY=77.4295 StartZ=0 EndX=-123.593 EndY=77.4151 EndZ=0
    g311: LineSegment StartX=-123.593 StartY=77.4151 StartZ=0 EndX=-123.039 EndY=77.3703 EndZ=0
    g312: LineSegment StartX=-24.7528 StartY=28.085 StartZ=0 EndX=-24.0876 EndY=27.9522 EndZ=0
    g313: LineSegment StartX=-7.86472 StartY=25.6369 StartZ=0 EndX=-6.8106 EndY=25.5322 EndZ=0
    g314: LineSegment StartX=-33.9547 StartY=-33.7057 StartZ=0 EndX=-33.9547 EndY=-33.706 EndZ=0
    g315: LineSegment StartX=-33.9547 StartY=-33.7047 StartZ=0 EndX=-33.9547 EndY=-33.7057 EndZ=0
    g316: LineSegment StartX=-33.9432 StartY=-33.4438 StartZ=0 EndX=-33.9547 EndY=-33.7047 EndZ=0
    g317: LineSegment StartX=-48.972 StartY=-39.5588 StartZ=0 EndX=-48.58 EndY=-39.863 EndZ=0
    g318: LineSegment StartX=-49.3086 StartY=-39.1941 StartZ=0 EndX=-48.972 EndY=-39.5588 EndZ=0
    g319: LineSegment StartX=-49.5804 StartY=-38.7789 StartZ=0 EndX=-49.3086 EndY=-39.1941 EndZ=0
    g320: LineSegment StartX=-49.78 StartY=-38.3245 StartZ=0 EndX=-49.5804 EndY=-38.7789 EndZ=0
    g321: LineSegment StartX=-49.9021 StartY=-37.8435 StartZ=0 EndX=-49.78 EndY=-38.3245 EndZ=0
    g322: LineSegment StartX=-49.9431 StartY=-37.3489 StartZ=0 EndX=-49.9021 EndY=-37.8435 EndZ=0
    g323: LineSegment StartX=-48.58 StartY=-39.863 StartZ=0 EndX=-48.1431 EndY=-40.0985 EndZ=0
    g324: LineSegment StartX=-34.066 StartY=-34.2933 StartZ=0 EndX=-34.118 EndY=-34.4527 EndZ=0
    g325: LineSegment StartX=-34.066 StartY=-34.2932 StartZ=0 EndX=-34.066 EndY=-34.2933 EndZ=0
    g326: LineSegment StartX=-34.118 StartY=-34.4528 StartZ=0 EndX=-34.1788 EndY=-34.6091 EndZ=0
    g327: LineSegment StartX=-34.118 StartY=-34.4527 StartZ=0 EndX=-34.118 EndY=-34.4528 EndZ=0
    g328: LineSegment StartX=-34.1789 StartY=-34.6092 StartZ=0 EndX=-34.2483 EndY=-34.7618 EndZ=0
    g329: LineSegment StartX=-34.1788 StartY=-34.6091 StartZ=0 EndX=-34.1789 EndY=-34.6092 EndZ=0
    g330: LineSegment StartX=-34.6209 StartY=-35.3429 StartZ=0 EndX=-34.7445 EndY=-35.4846 EndZ=0
    g331: LineSegment StartX=-34.6208 StartY=-35.3428 StartZ=0 EndX=-34.6209 EndY=-35.3429 EndZ=0
    g332: LineSegment StartX=-34.7447 StartY=-35.4849 StartZ=0 EndX=-34.9659 EndY=-35.6999 EndZ=0
    g333: LineSegment StartX=-34.7445 StartY=-35.4846 StartZ=0 EndX=-34.7447 EndY=-35.4849 EndZ=0
    g334: LineSegment StartX=-34.9662 StartY=-35.7001 StartZ=0 EndX=-35.2083 EndY=-35.8912 EndZ=0
    g335: LineSegment StartX=-34.9659 StartY=-35.6999 StartZ=0 EndX=-34.9662 EndY=-35.7001 EndZ=0
    g336: LineSegment StartX=-35.2087 StartY=-35.8915 StartZ=0 EndX=-35.4692 EndY=-36.0566 EndZ=0
    g337: LineSegment StartX=-35.2083 StartY=-35.8912 StartZ=0 EndX=-35.2087 EndY=-35.8915 EndZ=0
    g338: LineSegment StartX=-35.4692 StartY=-36.0566 StartZ=0 EndX=-35.7427 EndY=-36.1931 EndZ=0
    g339: LineSegment StartX=-35.7427 StartY=-36.1931 StartZ=0 EndX=-35.7431 EndY=-36.1933 EndZ=0
    g340: LineSegment StartX=-34.023 StartY=-34.131 StartZ=0 EndX=-34.023 EndY=-34.1311 EndZ=0
    g341: LineSegment StartX=-34.023 StartY=-34.1311 StartZ=0 EndX=-34.066 EndY=-34.2932 EndZ=0
    g342: LineSegment StartX=-33.9892 StartY=-33.9666 StartZ=0 EndX=-33.9892 EndY=-33.9667 EndZ=0
    g343: LineSegment StartX=-33.9892 StartY=-33.9667 StartZ=0 EndX=-34.023 EndY=-34.131 EndZ=0
    g344: LineSegment StartX=-33.9547 StartY=-33.706 StartZ=0 EndX=-33.9547 EndY=-33.7061 EndZ=0
    g345: LineSegment StartX=-33.9547 StartY=-33.7061 StartZ=0 EndX=-33.9892 EndY=-33.9666 EndZ=0
    g346: LineSegment StartX=-34.2483 StartY=-34.7618 StartZ=0 EndX=-34.2484 EndY=-34.7619 EndZ=0
    g347: LineSegment StartX=-34.2484 StartY=-34.7619 StartZ=0 EndX=-34.3262 EndY=-34.9104 EndZ=0
    g348: LineSegment StartX=-34.3262 StartY=-34.9104 StartZ=0 EndX=-34.3263 EndY=-34.9106 EndZ=0
    g349: LineSegment StartX=-34.3263 StartY=-34.9106 StartZ=0 EndX=-34.4123 EndY=-35.0545 EndZ=0
    g350: LineSegment StartX=-34.4123 StartY=-35.0545 StartZ=0 EndX=-34.4124 EndY=-35.0546 EndZ=0
    g351: LineSegment StartX=-34.4124 StartY=-35.0546 StartZ=0 EndX=-34.5063 EndY=-35.1935 EndZ=0
    g352: LineSegment StartX=-34.5063 StartY=-35.1935 StartZ=0 EndX=-34.5064 EndY=-35.1936 EndZ=0
    g353: LineSegment StartX=-34.5064 StartY=-35.1936 StartZ=0 EndX=-34.6208 EndY=-35.3428 EndZ=0
    g354: LineSegment StartX=-49.9431 StartY=-37.3489 StartZ=0 EndX=-49.9431 EndY=-36.6436 EndZ=0
    g355: LineSegment StartX=-33.9028 StartY=-33.3908 StartZ=0 EndX=-33.9432 EndY=-33.4437 EndZ=0
    g356: LineSegment StartX=-33.0013 StartY=-32.2112 StartZ=0 EndX=-33.9028 EndY=-33.3908 EndZ=0
    g357: LineSegment StartX=-32.8441 StartY=-32.0054 StartZ=0 EndX=-33.0013 EndY=-32.2112 EndZ=0
    g358: LineSegment StartX=-32.7124 StartY=-31.833 StartZ=0 EndX=-32.8441 EndY=-32.0054 EndZ=0
    g359: LineSegment StartX=-32.5498 StartY=-31.6202 StartZ=0 EndX=-32.7124 EndY=-31.833 EndZ=0
    g360: LineSegment StartX=-32.41 StartY=-31.4373 StartZ=0 EndX=-32.5498 EndY=-31.6202 EndZ=0
    g361: LineSegment StartX=-32.2462 StartY=-31.2229 StartZ=0 EndX=-32.41 EndY=-31.4373 EndZ=0
    g362: LineSegment StartX=-32.0985 StartY=-31.0297 StartZ=0 EndX=-32.2462 EndY=-31.2229 EndZ=0
    g363: LineSegment StartX=-31.9376 StartY=-30.819 StartZ=0 EndX=-32.0985 EndY=-31.0297 EndZ=0
    g364: LineSegment StartX=-31.7825 StartY=-30.616 StartZ=0 EndX=-31.9376 EndY=-30.819 EndZ=0
    g365: LineSegment StartX=-30.9431 StartY=-29.5175 StartZ=0 EndX=-31.7825 EndY=-30.616 EndZ=0
    g366: LineSegment StartX=-33.9432 StartY=-33.4437 StartZ=0 EndX=-33.9432 EndY=-33.4438 EndZ=0
    g367: LineSegment StartX=-33.9432 StartY=-33.4438 StartZ=0 EndX=-33.9432 EndY=-33.4438 EndZ=0
    g368: LineSegment StartX=-126.886 StartY=-74.6482 StartZ=0 EndX=-126.65 EndY=-74.9475 EndZ=0
    g369: LineSegment StartX=-127.139 StartY=-74.3887 StartZ=0 EndX=-126.886 EndY=-74.6482 EndZ=0
    g370: LineSegment StartX=-128.279 StartY=74.1274 StartZ=0 EndX=-128.344 EndY=74.1464 EndZ=0
    g371: LineSegment StartX=-128.344 StartY=74.1464 StartZ=0 EndX=-128.44 EndY=74.189 EndZ=0
    g372: LineSegment StartX=-128.114 StartY=74.0894 StartZ=0 EndX=-128.18 EndY=74.0989 EndZ=0
    g373: LineSegment StartX=-128.18 StartY=74.0989 StartZ=0 EndX=-128.279 EndY=74.1274 EndZ=0
    g374: LineSegment StartX=-127.95 StartY=74.0751 StartZ=0 EndX=-128.015 EndY=74.0752 EndZ=0
    g375: LineSegment StartX=-128.015 StartY=74.0752 StartZ=0 EndX=-128.114 EndY=74.0894 EndZ=0
    g376: LineSegment StartX=-127.789 StartY=74.0839 StartZ=0 EndX=-127.852 EndY=74.075 EndZ=0
    g377: LineSegment StartX=-127.852 StartY=74.075 StartZ=0 EndX=-127.95 EndY=74.0751 EndZ=0
    g378: LineSegment StartX=-127.634 StartY=74.1146 StartZ=0 EndX=-127.694 EndY=74.0972 EndZ=0
    g379: LineSegment StartX=-127.694 StartY=74.0972 StartZ=0 EndX=-127.789 EndY=74.0839 EndZ=0
    g380: LineSegment StartX=-127.486 StartY=74.166 StartZ=0 EndX=-127.543 EndY=74.1408 EndZ=0
    g381: LineSegment StartX=-127.543 StartY=74.1408 StartZ=0 EndX=-127.634 EndY=74.1146 EndZ=0
    g382: LineSegment StartX=-126.65 StartY=74.9471 StartZ=0 EndX=-126.662 EndY=74.9328 EndZ=0
    g383: LineSegment StartX=-126.662 StartY=74.9328 StartZ=0 EndX=-127.025 EndY=74.4913 EndZ=0
    g384: LineSegment StartX=-129.046 StartY=-74.7537 StartZ=0 EndX=-129.135 EndY=-74.9351 EndZ=0
    g385: LineSegment StartX=-128.933 StartY=-74.5857 StartZ=0 EndX=-129.046 EndY=-74.7537 EndZ=0
    g386: LineSegment StartX=-128.477 StartY=-74.2076 StartZ=0 EndX=-128.645 EndY=-74.3088 EndZ=0
    g387: LineSegment StartX=-128.299 StartY=-74.1346 StartZ=0 EndX=-128.477 EndY=-74.2076 EndZ=0
    g388: LineSegment StartX=-128.117 StartY=-74.0907 StartZ=0 EndX=-128.299 EndY=-74.1346 EndZ=0
    g389: LineSegment StartX=-127.934 StartY=-74.0759 StartZ=0 EndX=-128.117 EndY=-74.0907 EndZ=0
    g390: LineSegment StartX=-127.277 StartY=-74.282 StartZ=0 EndX=-127.426 EndY=-74.1948 EndZ=0
    g391: LineSegment StartX=-127.426 StartY=-74.1948 StartZ=0 EndX=-127.586 EndY=-74.1298 EndZ=0
    g392: LineSegment StartX=-127.586 StartY=-74.1298 StartZ=0 EndX=-127.756 EndY=-74.0895 EndZ=0
    g393: LineSegment StartX=-127.756 StartY=-74.0895 StartZ=0 EndX=-127.934 EndY=-74.0759 EndZ=0
    g394: LineSegment StartX=-127.139 StartY=-74.3887 StartZ=0 EndX=-127.277 EndY=-74.282 EndZ=0
    g395: LineSegment StartX=-128.645 StartY=-74.3088 StartZ=0 EndX=-128.798 EndY=-74.4359 EndZ=0
    g396: LineSegment StartX=-128.798 StartY=-74.4359 StartZ=0 EndX=-128.933 EndY=-74.5857 EndZ=0
    g397: LineSegment StartX=-129.135 StartY=-74.9351 StartZ=0 EndX=-129.197 EndY=-75.1246 EndZ=0
    g398: LineSegment StartX=-129.197 StartY=-75.1246 StartZ=0 EndX=-129.232 EndY=-75.3173 EndZ=0
    g399: LineSegment StartX=-129.232 StartY=-75.3173 StartZ=0 EndX=-129.24 EndY=-75.5084 EndZ=0
    ... +558 more geometry lines
  constraints (28):
    c: Vertical(g354)
    c: Vertical(g366)
    c: Vertical(g367)
    c: Horizontal(g460)
    c: Horizontal(g461)
    c: Horizontal(g498)
    c: Horizontal(g499)
    c: Vertical(g504)
    c: Vertical(g505)
    c: Vertical(g506)
    c: Vertical(g543)
    c: Vertical(g544)
    c: Vertical(g545)
    c: Vertical(g546)
    c: Vertical(g689)
    c: Horizontal(g692)
    c: Vertical(g907)
    c: Vertical(g908)
    c: Vertical(g940)
    c: Vertical(g941)
    c: Vertical(g942)
    c: Vertical(g943)
    c: Vertical(g944)
    c: Vertical(g945)
    c: Vertical(g946)
    c: Vertical(g947)
    c: Vertical(g956)
    c: Vertical(g957)
